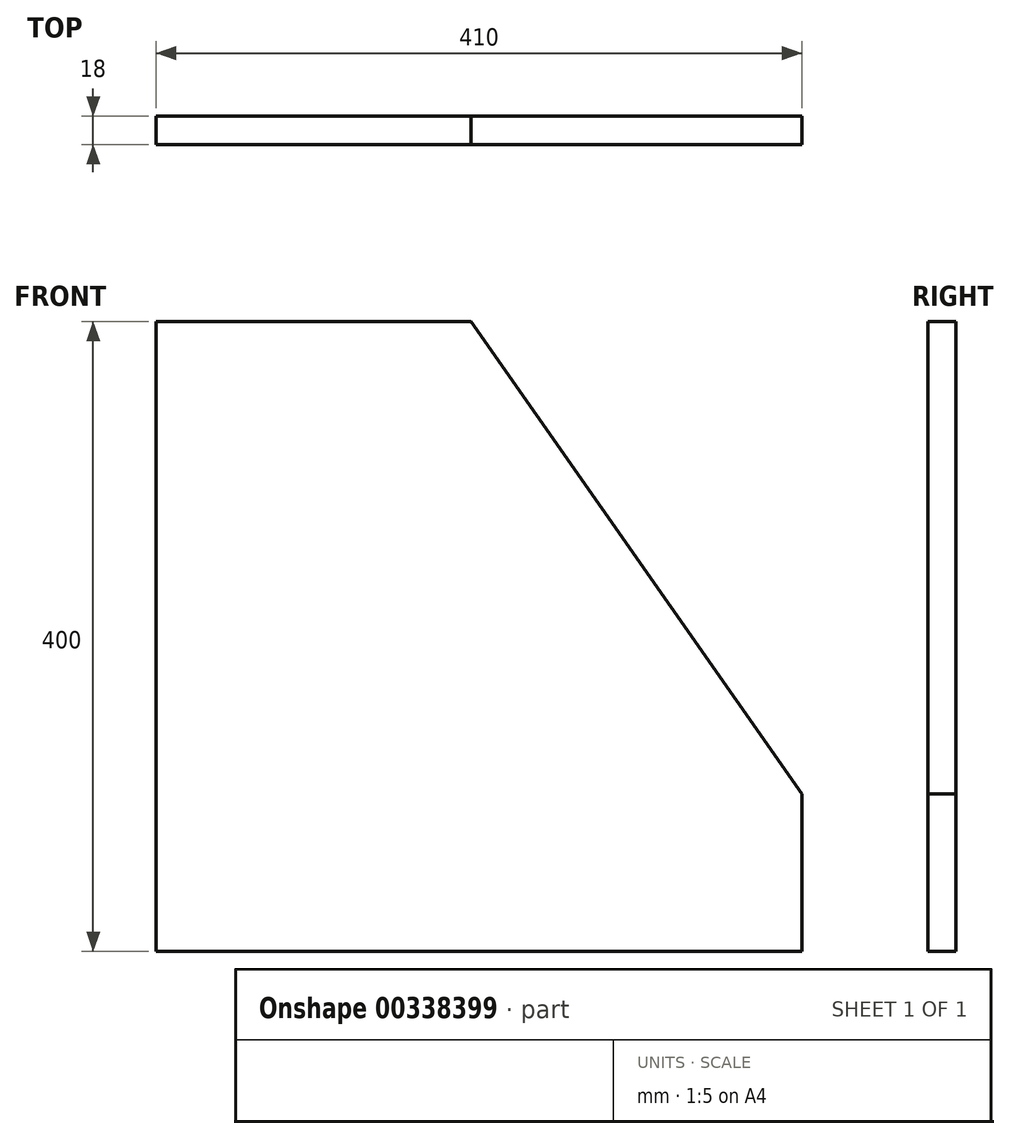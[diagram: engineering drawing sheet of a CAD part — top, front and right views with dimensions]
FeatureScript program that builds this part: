
annotation { "Feature Type Name" : "Feature", "Feature Type Description" : "" }
export const myFeature = defineFeature(function(context is Context, id is Id, definition is map)
    precondition{}
    {
        {
            var Q0;
            Q0=qCreatedBy(makeId("Front.planeOp"),FACE);
            var sketch = newSketch(context, id + "F0", { "sketchPlane" : qUnion([Q0])});
            skLineSegment(sketch, "E0.bottom", {"start": v(-100, -200) * mm, "end": v(100, -200) * mm});
            skLineSegment(sketch, "E0.top", {"start": v(-100, 200) * mm, "end": v(100, 200) * mm});
            skLineSegment(sketch, "E0.right", {"start": v(100, -100) * mm, "end": v(100, 200) * mm});
            skPoint(sketch, "E0.middle", {"position": v(0, 0) * mm});
            skLineSegment(sketch, "E1.bottom", {"start": v(100, -200) * mm, "end": v(310, -200) * mm});
            skLineSegment(sketch, "E1.top", {"start": v(100, -100) * mm, "end": v(310, -100) * mm});
            skLineSegment(sketch, "E1.right", {"start": v(310, -200) * mm, "end": v(310, -100) * mm});
            skLineSegment(sketch, "E2", {"start": v(100, 200) * mm, "end": v(310, -100) * mm});
            skLineSegment(sketch, "E3", {"start": v(-100, 200) * mm, "end": v(-100, -200) * mm});
            skSolve(sketch);
        }
        {
            var Q0;
            Q0=makeQuery(id+"F0.imprint","IMPRINT",FACE,{"disambiguationData":[TD([[makeQuery(id+"F0.imprint","IMPRINT",EDGE,{"derivedFrom":sQuery(id+"F0.wireOp",EDGE,"E0.right")}),-1.0]])]});
            var Q1;
            Q1=makeQuery(id+"F0.imprint","IMPRINT",FACE,{"disambiguationData":[TD([[makeQuery(id+"F0.imprint","IMPRINT",EDGE,{"derivedFrom":sQuery(id+"F0.wireOp",EDGE,"E0.bottom")}),1.0]])]});
            var Q2;
            Q2=makeQuery(id+"F0.imprint","IMPRINT",FACE,{"disambiguationData":[TD([[makeQuery(id+"F0.imprint","IMPRINT",EDGE,{"derivedFrom":sQuery(id+"F0.wireOp",EDGE,"E0.left")}),1.0]])]});
            extrude(context, id + "F1", {"entities" : qUnion([Q0, Q1, Q2]), "depth" : 18 * mm});
        }
    });
